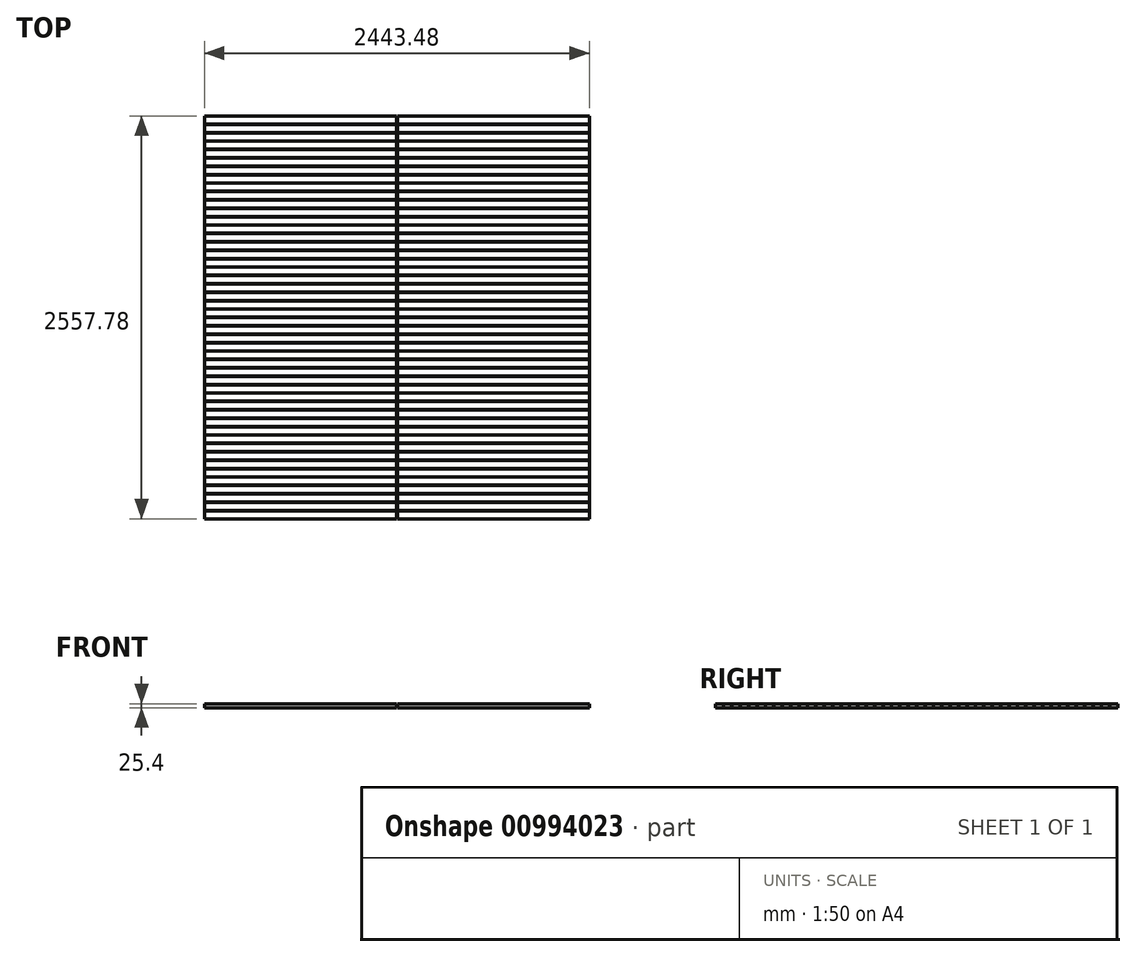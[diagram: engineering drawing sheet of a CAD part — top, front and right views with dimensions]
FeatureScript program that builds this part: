
annotation { "Feature Type Name" : "Feature", "Feature Type Description" : "" }
export const myFeature = defineFeature(function(context is Context, id is Id, definition is map)
    precondition{}
    {
        {
            var Q0;
            Q0=qCreatedBy(makeId("Top.planeOp"),FACE);
            var sketch = newSketch(context, id + "F0", { "sketchPlane" : qUnion([Q0])});
            skLineSegment(sketch, "E0", {"start": v(0, 0) * mm, "end": v(0, 2540) * mm});
            skLineSegment(sketch, "E1.bottom", {"start": v(-1221.74, 2548.89) * mm, "end": v(-2.54, 2548.89) * mm});
            skLineSegment(sketch, "E1.top", {"start": v(-1221.74, 2498.09) * mm, "end": v(-2.54, 2498.09) * mm});
            skLineSegment(sketch, "E1.left", {"start": v(-1221.74, 2548.89) * mm, "end": v(-1221.74, 2498.09) * mm});
            skLineSegment(sketch, "E1.right", {"start": v(-2.54, 2548.89) * mm, "end": v(-2.54, 2498.09) * mm});
            skLineSegment(sketch, "E2.0.1.0", {"start": v(-1221.74, 2495.55) * mm, "end": v(-1221.74, 2444.75) * mm});
            skLineSegment(sketch, "E2.0.1.1", {"start": v(-2.54, 2495.55) * mm, "end": v(-2.54, 2444.75) * mm});
            skLineSegment(sketch, "E2.0.1.2", {"start": v(-1221.74, 2495.55) * mm, "end": v(-2.54, 2495.55) * mm});
            skLineSegment(sketch, "E2.0.1.3", {"start": v(-1221.74, 2444.75) * mm, "end": v(-2.54, 2444.75) * mm});
            skLineSegment(sketch, "E2.0.2.0", {"start": v(-1221.74, 2442.2) * mm, "end": v(-1221.74, 2391.4) * mm});
            skLineSegment(sketch, "E2.0.2.1", {"start": v(-2.54, 2442.2) * mm, "end": v(-2.54, 2391.4) * mm});
            skLineSegment(sketch, "E2.0.2.2", {"start": v(-1221.74, 2442.2) * mm, "end": v(-2.54, 2442.2) * mm});
            skLineSegment(sketch, "E2.0.2.3", {"start": v(-1221.74, 2391.4) * mm, "end": v(-2.54, 2391.4) * mm});
            skLineSegment(sketch, "E2.0.3.0", {"start": v(-1221.74, 2388.87) * mm, "end": v(-1221.74, 2338.07) * mm});
            skLineSegment(sketch, "E2.0.3.1", {"start": v(-2.54, 2388.87) * mm, "end": v(-2.54, 2338.07) * mm});
            skLineSegment(sketch, "E2.0.3.2", {"start": v(-1221.74, 2388.87) * mm, "end": v(-2.54, 2388.87) * mm});
            skLineSegment(sketch, "E2.0.3.3", {"start": v(-1221.74, 2338.07) * mm, "end": v(-2.54, 2338.07) * mm});
            skLineSegment(sketch, "E2.0.4.0", {"start": v(-1221.74, 2335.53) * mm, "end": v(-1221.74, 2284.73) * mm});
            skLineSegment(sketch, "E2.0.4.1", {"start": v(-2.54, 2335.53) * mm, "end": v(-2.54, 2284.73) * mm});
            skLineSegment(sketch, "E2.0.4.2", {"start": v(-1221.74, 2335.53) * mm, "end": v(-2.54, 2335.53) * mm});
            skLineSegment(sketch, "E2.0.4.3", {"start": v(-1221.74, 2284.73) * mm, "end": v(-2.54, 2284.73) * mm});
            skLineSegment(sketch, "E2.0.5.0", {"start": v(-1221.74, 2282.2) * mm, "end": v(-1221.74, 2231.39) * mm});
            skLineSegment(sketch, "E2.0.5.1", {"start": v(-2.54, 2282.2) * mm, "end": v(-2.54, 2231.39) * mm});
            skLineSegment(sketch, "E2.0.5.2", {"start": v(-1221.74, 2282.2) * mm, "end": v(-2.54, 2282.2) * mm});
            skLineSegment(sketch, "E2.0.5.3", {"start": v(-1221.74, 2231.39) * mm, "end": v(-2.54, 2231.39) * mm});
            skLineSegment(sketch, "E2.0.6.0", {"start": v(-1221.74, 2228.85) * mm, "end": v(-1221.74, 2178.05) * mm});
            skLineSegment(sketch, "E2.0.6.1", {"start": v(-2.54, 2228.85) * mm, "end": v(-2.54, 2178.05) * mm});
            skLineSegment(sketch, "E2.0.6.2", {"start": v(-1221.74, 2228.85) * mm, "end": v(-2.54, 2228.85) * mm});
            skLineSegment(sketch, "E2.0.6.3", {"start": v(-1221.74, 2178.05) * mm, "end": v(-2.54, 2178.05) * mm});
            skLineSegment(sketch, "E2.0.7.0", {"start": v(-1221.74, 2175.51) * mm, "end": v(-1221.74, 2124.7) * mm});
            skLineSegment(sketch, "E2.0.7.1", {"start": v(-2.54, 2175.51) * mm, "end": v(-2.54, 2124.7) * mm});
            skLineSegment(sketch, "E2.0.7.2", {"start": v(-1221.74, 2175.51) * mm, "end": v(-2.54, 2175.51) * mm});
            skLineSegment(sketch, "E2.0.7.3", {"start": v(-1221.74, 2124.7) * mm, "end": v(-2.54, 2124.7) * mm});
            skLineSegment(sketch, "E2.0.8.0", {"start": v(-1221.74, 2122.17) * mm, "end": v(-1221.74, 2071.37) * mm});
            skLineSegment(sketch, "E2.0.8.1", {"start": v(-2.54, 2122.17) * mm, "end": v(-2.54, 2071.37) * mm});
            skLineSegment(sketch, "E2.0.8.2", {"start": v(-1221.74, 2122.17) * mm, "end": v(-2.54, 2122.17) * mm});
            skLineSegment(sketch, "E2.0.8.3", {"start": v(-1221.74, 2071.37) * mm, "end": v(-2.54, 2071.37) * mm});
            skLineSegment(sketch, "E2.0.9.0", {"start": v(-1221.74, 2068.83) * mm, "end": v(-1221.74, 2018.03) * mm});
            skLineSegment(sketch, "E2.0.9.1", {"start": v(-2.54, 2068.83) * mm, "end": v(-2.54, 2018.03) * mm});
            skLineSegment(sketch, "E2.0.9.2", {"start": v(-1221.74, 2068.83) * mm, "end": v(-2.54, 2068.83) * mm});
            skLineSegment(sketch, "E2.0.9.3", {"start": v(-1221.74, 2018.03) * mm, "end": v(-2.54, 2018.03) * mm});
            skLineSegment(sketch, "E2.0.10.0", {"start": v(-1221.74, 2015.5) * mm, "end": v(-1221.74, 1964.69) * mm});
            skLineSegment(sketch, "E2.0.10.1", {"start": v(-2.54, 2015.5) * mm, "end": v(-2.54, 1964.69) * mm});
            skLineSegment(sketch, "E2.0.10.2", {"start": v(-1221.74, 2015.5) * mm, "end": v(-2.54, 2015.5) * mm});
            skLineSegment(sketch, "E2.0.10.3", {"start": v(-1221.74, 1964.69) * mm, "end": v(-2.54, 1964.7) * mm});
            skLineSegment(sketch, "E2.0.11.0", {"start": v(-1221.74, 1962.15) * mm, "end": v(-1221.74, 1911.35) * mm});
            skLineSegment(sketch, "E2.0.11.1", {"start": v(-2.54, 1962.15) * mm, "end": v(-2.54, 1911.35) * mm});
            skLineSegment(sketch, "E2.0.11.2", {"start": v(-1221.74, 1962.15) * mm, "end": v(-2.54, 1962.15) * mm});
            skLineSegment(sketch, "E2.0.11.3", {"start": v(-1221.74, 1911.35) * mm, "end": v(-2.54, 1911.35) * mm});
            skLineSegment(sketch, "E2.0.12.0", {"start": v(-1221.74, 1908.81) * mm, "end": v(-1221.74, 1858) * mm});
            skLineSegment(sketch, "E2.0.12.1", {"start": v(-2.54, 1908.81) * mm, "end": v(-2.54, 1858) * mm});
            skLineSegment(sketch, "E2.0.12.2", {"start": v(-1221.74, 1908.81) * mm, "end": v(-2.54, 1908.81) * mm});
            skLineSegment(sketch, "E2.0.12.3", {"start": v(-1221.74, 1858) * mm, "end": v(-2.54, 1858.01) * mm});
            skLineSegment(sketch, "E2.0.13.0", {"start": v(-1221.74, 1855.47) * mm, "end": v(-1221.74, 1804.67) * mm});
            skLineSegment(sketch, "E2.0.13.1", {"start": v(-2.54, 1855.47) * mm, "end": v(-2.54, 1804.67) * mm});
            skLineSegment(sketch, "E2.0.13.2", {"start": v(-1221.74, 1855.47) * mm, "end": v(-2.54, 1855.47) * mm});
            skLineSegment(sketch, "E2.0.13.3", {"start": v(-1221.74, 1804.67) * mm, "end": v(-2.54, 1804.67) * mm});
            skLineSegment(sketch, "E2.0.14.0", {"start": v(-1221.74, 1802.13) * mm, "end": v(-1221.74, 1751.33) * mm});
            skLineSegment(sketch, "E2.0.14.1", {"start": v(-2.54, 1802.13) * mm, "end": v(-2.54, 1751.33) * mm});
            skLineSegment(sketch, "E2.0.14.2", {"start": v(-1221.74, 1802.13) * mm, "end": v(-2.54, 1802.13) * mm});
            skLineSegment(sketch, "E2.0.14.3", {"start": v(-1221.74, 1751.33) * mm, "end": v(-2.54, 1751.33) * mm});
            skLineSegment(sketch, "E2.0.15.0", {"start": v(-1221.74, 1748.8) * mm, "end": v(-1221.74, 1698) * mm});
            skLineSegment(sketch, "E2.0.15.1", {"start": v(-2.54, 1748.8) * mm, "end": v(-2.54, 1698) * mm});
            skLineSegment(sketch, "E2.0.15.2", {"start": v(-1221.74, 1748.8) * mm, "end": v(-2.54, 1748.8) * mm});
            skLineSegment(sketch, "E2.0.15.3", {"start": v(-1221.74, 1698) * mm, "end": v(-2.54, 1698) * mm});
            skLineSegment(sketch, "E2.0.16.0", {"start": v(-1221.74, 1695.45) * mm, "end": v(-1221.74, 1644.65) * mm});
            skLineSegment(sketch, "E2.0.16.1", {"start": v(-2.54, 1695.45) * mm, "end": v(-2.54, 1644.65) * mm});
            skLineSegment(sketch, "E2.0.16.2", {"start": v(-1221.74, 1695.45) * mm, "end": v(-2.54, 1695.45) * mm});
            skLineSegment(sketch, "E2.0.16.3", {"start": v(-1221.74, 1644.65) * mm, "end": v(-2.54, 1644.65) * mm});
            skLineSegment(sketch, "E2.0.17.0", {"start": v(-1221.74, 1642.11) * mm, "end": v(-1221.74, 1591.31) * mm});
            skLineSegment(sketch, "E2.0.17.1", {"start": v(-2.54, 1642.11) * mm, "end": v(-2.54, 1591.31) * mm});
            skLineSegment(sketch, "E2.0.17.2", {"start": v(-1221.74, 1642.11) * mm, "end": v(-2.54, 1642.11) * mm});
            skLineSegment(sketch, "E2.0.17.3", {"start": v(-1221.74, 1591.31) * mm, "end": v(-2.54, 1591.31) * mm});
            skLineSegment(sketch, "E2.0.18.0", {"start": v(-1221.74, 1588.77) * mm, "end": v(-1221.74, 1537.97) * mm});
            skLineSegment(sketch, "E2.0.18.1", {"start": v(-2.54, 1588.77) * mm, "end": v(-2.54, 1537.97) * mm});
            skLineSegment(sketch, "E2.0.18.2", {"start": v(-1221.74, 1588.77) * mm, "end": v(-2.54, 1588.77) * mm});
            skLineSegment(sketch, "E2.0.18.3", {"start": v(-1221.74, 1537.97) * mm, "end": v(-2.54, 1537.97) * mm});
            skLineSegment(sketch, "E2.0.19.0", {"start": v(-1221.74, 1535.43) * mm, "end": v(-1221.74, 1484.63) * mm});
            skLineSegment(sketch, "E2.0.19.1", {"start": v(-2.54, 1535.43) * mm, "end": v(-2.54, 1484.63) * mm});
            skLineSegment(sketch, "E2.0.19.2", {"start": v(-1221.74, 1535.43) * mm, "end": v(-2.54, 1535.43) * mm});
            skLineSegment(sketch, "E2.0.19.3", {"start": v(-1221.74, 1484.63) * mm, "end": v(-2.54, 1484.63) * mm});
            skLineSegment(sketch, "E2.0.20.0", {"start": v(-1221.74, 1482.1) * mm, "end": v(-1221.74, 1431.3) * mm});
            skLineSegment(sketch, "E2.0.20.1", {"start": v(-2.54, 1482.1) * mm, "end": v(-2.54, 1431.3) * mm});
            skLineSegment(sketch, "E2.0.20.2", {"start": v(-1221.74, 1482.1) * mm, "end": v(-2.54, 1482.1) * mm});
            skLineSegment(sketch, "E2.0.20.3", {"start": v(-1221.74, 1431.3) * mm, "end": v(-2.54, 1431.3) * mm});
            skLineSegment(sketch, "E2.0.21.0", {"start": v(-1221.74, 1428.75) * mm, "end": v(-1221.74, 1377.95) * mm});
            skLineSegment(sketch, "E2.0.21.1", {"start": v(-2.54, 1428.75) * mm, "end": v(-2.54, 1377.95) * mm});
            skLineSegment(sketch, "E2.0.21.2", {"start": v(-1221.74, 1428.75) * mm, "end": v(-2.54, 1428.75) * mm});
            skLineSegment(sketch, "E2.0.21.3", {"start": v(-1221.74, 1377.95) * mm, "end": v(-2.54, 1377.95) * mm});
            skLineSegment(sketch, "E2.0.22.0", {"start": v(-1221.74, 1375.41) * mm, "end": v(-1221.74, 1324.61) * mm});
            skLineSegment(sketch, "E2.0.22.1", {"start": v(-2.54, 1375.41) * mm, "end": v(-2.54, 1324.61) * mm});
            skLineSegment(sketch, "E2.0.22.2", {"start": v(-1221.74, 1375.41) * mm, "end": v(-2.54, 1375.41) * mm});
            skLineSegment(sketch, "E2.0.22.3", {"start": v(-1221.74, 1324.61) * mm, "end": v(-2.54, 1324.61) * mm});
            skLineSegment(sketch, "E2.0.23.0", {"start": v(-1221.74, 1322.07) * mm, "end": v(-1221.74, 1271.27) * mm});
            skLineSegment(sketch, "E2.0.23.1", {"start": v(-2.54, 1322.07) * mm, "end": v(-2.54, 1271.27) * mm});
            skLineSegment(sketch, "E2.0.23.2", {"start": v(-1221.74, 1322.07) * mm, "end": v(-2.54, 1322.07) * mm});
            skLineSegment(sketch, "E2.0.23.3", {"start": v(-1221.74, 1271.27) * mm, "end": v(-2.54, 1271.27) * mm});
            skLineSegment(sketch, "E2.0.24.0", {"start": v(-1221.74, 1268.73) * mm, "end": v(-1221.74, 1217.93) * mm});
            skLineSegment(sketch, "E2.0.24.1", {"start": v(-2.54, 1268.73) * mm, "end": v(-2.54, 1217.93) * mm});
            skLineSegment(sketch, "E2.0.24.2", {"start": v(-1221.74, 1268.73) * mm, "end": v(-2.54, 1268.73) * mm});
            skLineSegment(sketch, "E2.0.24.3", {"start": v(-1221.74, 1217.93) * mm, "end": v(-2.54, 1217.93) * mm});
            skLineSegment(sketch, "E2.0.25.0", {"start": v(-1221.74, 1215.4) * mm, "end": v(-1221.74, 1164.6) * mm});
            skLineSegment(sketch, "E2.0.25.1", {"start": v(-2.54, 1215.4) * mm, "end": v(-2.54, 1164.6) * mm});
            skLineSegment(sketch, "E2.0.25.2", {"start": v(-1221.74, 1215.4) * mm, "end": v(-2.54, 1215.4) * mm});
            skLineSegment(sketch, "E2.0.25.3", {"start": v(-1221.74, 1164.6) * mm, "end": v(-2.54, 1164.6) * mm});
            skLineSegment(sketch, "E2.0.26.0", {"start": v(-1221.74, 1162.05) * mm, "end": v(-1221.74, 1111.25) * mm});
            skLineSegment(sketch, "E2.0.26.1", {"start": v(-2.54, 1162.05) * mm, "end": v(-2.54, 1111.25) * mm});
            skLineSegment(sketch, "E2.0.26.2", {"start": v(-1221.74, 1162.05) * mm, "end": v(-2.54, 1162.05) * mm});
            skLineSegment(sketch, "E2.0.26.3", {"start": v(-1221.74, 1111.25) * mm, "end": v(-2.54, 1111.25) * mm});
            skLineSegment(sketch, "E2.0.27.0", {"start": v(-1221.74, 1108.71) * mm, "end": v(-1221.74, 1057.91) * mm});
            skLineSegment(sketch, "E2.0.27.1", {"start": v(-2.54, 1108.71) * mm, "end": v(-2.54, 1057.91) * mm});
            skLineSegment(sketch, "E2.0.27.2", {"start": v(-1221.74, 1108.71) * mm, "end": v(-2.54, 1108.71) * mm});
            skLineSegment(sketch, "E2.0.27.3", {"start": v(-1221.74, 1057.91) * mm, "end": v(-2.54, 1057.91) * mm});
            skLineSegment(sketch, "E2.0.28.0", {"start": v(-1221.74, 1055.37) * mm, "end": v(-1221.74, 1004.57) * mm});
            skLineSegment(sketch, "E2.0.28.1", {"start": v(-2.54, 1055.37) * mm, "end": v(-2.54, 1004.57) * mm});
            skLineSegment(sketch, "E2.0.28.2", {"start": v(-1221.74, 1055.37) * mm, "end": v(-2.54, 1055.37) * mm});
            skLineSegment(sketch, "E2.0.28.3", {"start": v(-1221.74, 1004.57) * mm, "end": v(-2.54, 1004.57) * mm});
            skLineSegment(sketch, "E2.0.29.0", {"start": v(-1221.74, 1002.03) * mm, "end": v(-1221.74, 951.23) * mm});
            skLineSegment(sketch, "E2.0.29.1", {"start": v(-2.54, 1002.03) * mm, "end": v(-2.54, 951.23) * mm});
            skLineSegment(sketch, "E2.0.29.2", {"start": v(-1221.74, 1002.03) * mm, "end": v(-2.54, 1002.03) * mm});
            skLineSegment(sketch, "E2.0.29.3", {"start": v(-1221.74, 951.23) * mm, "end": v(-2.54, 951.23) * mm});
            skLineSegment(sketch, "E2.0.30.0", {"start": v(-1221.74, 948.7) * mm, "end": v(-1221.74, 897.9) * mm});
            skLineSegment(sketch, "E2.0.30.1", {"start": v(-2.54, 948.7) * mm, "end": v(-2.54, 897.9) * mm});
            skLineSegment(sketch, "E2.0.30.2", {"start": v(-1221.74, 948.7) * mm, "end": v(-2.54, 948.7) * mm});
            skLineSegment(sketch, "E2.0.30.3", {"start": v(-1221.74, 897.9) * mm, "end": v(-2.54, 897.9) * mm});
            skLineSegment(sketch, "E2.0.31.0", {"start": v(-1221.74, 895.35) * mm, "end": v(-1221.74, 844.55) * mm});
            skLineSegment(sketch, "E2.0.31.1", {"start": v(-2.54, 895.35) * mm, "end": v(-2.54, 844.55) * mm});
            skLineSegment(sketch, "E2.0.31.2", {"start": v(-1221.74, 895.35) * mm, "end": v(-2.54, 895.35) * mm});
            skLineSegment(sketch, "E2.0.31.3", {"start": v(-1221.74, 844.55) * mm, "end": v(-2.54, 844.55) * mm});
            skLineSegment(sketch, "E2.0.32.0", {"start": v(-1221.74, 842.01) * mm, "end": v(-1221.74, 791.21) * mm});
            skLineSegment(sketch, "E2.0.32.1", {"start": v(-2.54, 842.01) * mm, "end": v(-2.54, 791.21) * mm});
            skLineSegment(sketch, "E2.0.32.2", {"start": v(-1221.74, 842.01) * mm, "end": v(-2.54, 842.01) * mm});
            skLineSegment(sketch, "E2.0.32.3", {"start": v(-1221.74, 791.21) * mm, "end": v(-2.54, 791.21) * mm});
            skLineSegment(sketch, "E2.0.33.0", {"start": v(-1221.74, 788.67) * mm, "end": v(-1221.74, 737.87) * mm});
            skLineSegment(sketch, "E2.0.33.1", {"start": v(-2.54, 788.67) * mm, "end": v(-2.54, 737.87) * mm});
            skLineSegment(sketch, "E2.0.33.2", {"start": v(-1221.74, 788.67) * mm, "end": v(-2.54, 788.67) * mm});
            skLineSegment(sketch, "E2.0.33.3", {"start": v(-1221.74, 737.87) * mm, "end": v(-2.54, 737.87) * mm});
            skLineSegment(sketch, "E2.0.34.0", {"start": v(-1221.74, 735.33) * mm, "end": v(-1221.74, 684.53) * mm});
            skLineSegment(sketch, "E2.0.34.1", {"start": v(-2.54, 735.33) * mm, "end": v(-2.54, 684.53) * mm});
            skLineSegment(sketch, "E2.0.34.2", {"start": v(-1221.74, 735.33) * mm, "end": v(-2.54, 735.33) * mm});
            skLineSegment(sketch, "E2.0.34.3", {"start": v(-1221.74, 684.53) * mm, "end": v(-2.54, 684.53) * mm});
            skLineSegment(sketch, "E2.0.35.0", {"start": v(-1221.74, 682) * mm, "end": v(-1221.74, 631.2) * mm});
            skLineSegment(sketch, "E2.0.35.1", {"start": v(-2.54, 682) * mm, "end": v(-2.54, 631.2) * mm});
            skLineSegment(sketch, "E2.0.35.2", {"start": v(-1221.74, 682) * mm, "end": v(-2.54, 682) * mm});
            skLineSegment(sketch, "E2.0.35.3", {"start": v(-1221.74, 631.2) * mm, "end": v(-2.54, 631.2) * mm});
            skLineSegment(sketch, "E2.0.36.0", {"start": v(-1221.74, 628.65) * mm, "end": v(-1221.74, 577.85) * mm});
            skLineSegment(sketch, "E2.0.36.1", {"start": v(-2.54, 628.65) * mm, "end": v(-2.54, 577.85) * mm});
            skLineSegment(sketch, "E2.0.36.2", {"start": v(-1221.74, 628.65) * mm, "end": v(-2.54, 628.65) * mm});
            skLineSegment(sketch, "E2.0.36.3", {"start": v(-1221.74, 577.85) * mm, "end": v(-2.54, 577.85) * mm});
            skLineSegment(sketch, "E2.0.37.0", {"start": v(-1221.74, 575.31) * mm, "end": v(-1221.74, 524.51) * mm});
            skLineSegment(sketch, "E2.0.37.1", {"start": v(-2.54, 575.31) * mm, "end": v(-2.54, 524.51) * mm});
            skLineSegment(sketch, "E2.0.37.2", {"start": v(-1221.74, 575.31) * mm, "end": v(-2.54, 575.31) * mm});
            skLineSegment(sketch, "E2.0.37.3", {"start": v(-1221.74, 524.51) * mm, "end": v(-2.54, 524.51) * mm});
            skLineSegment(sketch, "E2.0.38.0", {"start": v(-1221.74, 521.97) * mm, "end": v(-1221.74, 471.17) * mm});
            skLineSegment(sketch, "E2.0.38.1", {"start": v(-2.54, 521.97) * mm, "end": v(-2.54, 471.17) * mm});
            skLineSegment(sketch, "E2.0.38.2", {"start": v(-1221.74, 521.97) * mm, "end": v(-2.54, 521.97) * mm});
            skLineSegment(sketch, "E2.0.38.3", {"start": v(-1221.74, 471.17) * mm, "end": v(-2.54, 471.17) * mm});
            skLineSegment(sketch, "E2.0.39.0", {"start": v(-1221.74, 468.63) * mm, "end": v(-1221.74, 417.83) * mm});
            skLineSegment(sketch, "E2.0.39.1", {"start": v(-2.54, 468.63) * mm, "end": v(-2.54, 417.83) * mm});
            skLineSegment(sketch, "E2.0.39.2", {"start": v(-1221.74, 468.63) * mm, "end": v(-2.54, 468.63) * mm});
            skLineSegment(sketch, "E2.0.39.3", {"start": v(-1221.74, 417.83) * mm, "end": v(-2.54, 417.83) * mm});
            skLineSegment(sketch, "E2.0.40.0", {"start": v(-1221.74, 415.3) * mm, "end": v(-1221.74, 364.5) * mm});
            skLineSegment(sketch, "E2.0.40.1", {"start": v(-2.54, 415.3) * mm, "end": v(-2.54, 364.5) * mm});
            skLineSegment(sketch, "E2.0.40.2", {"start": v(-1221.74, 415.3) * mm, "end": v(-2.54, 415.3) * mm});
            skLineSegment(sketch, "E2.0.40.3", {"start": v(-1221.74, 364.5) * mm, "end": v(-2.54, 364.5) * mm});
            skLineSegment(sketch, "E2.0.41.0", {"start": v(-1221.74, 361.95) * mm, "end": v(-1221.74, 311.15) * mm});
            skLineSegment(sketch, "E2.0.41.1", {"start": v(-2.54, 361.95) * mm, "end": v(-2.54, 311.15) * mm});
            skLineSegment(sketch, "E2.0.41.2", {"start": v(-1221.74, 361.95) * mm, "end": v(-2.54, 361.95) * mm});
            skLineSegment(sketch, "E2.0.41.3", {"start": v(-1221.74, 311.15) * mm, "end": v(-2.54, 311.15) * mm});
            skLineSegment(sketch, "E2.0.42.0", {"start": v(-1221.74, 308.61) * mm, "end": v(-1221.74, 257.81) * mm});
            skLineSegment(sketch, "E2.0.42.1", {"start": v(-2.54, 308.61) * mm, "end": v(-2.54, 257.81) * mm});
            skLineSegment(sketch, "E2.0.42.2", {"start": v(-1221.74, 308.61) * mm, "end": v(-2.54, 308.61) * mm});
            skLineSegment(sketch, "E2.0.42.3", {"start": v(-1221.74, 257.81) * mm, "end": v(-2.54, 257.81) * mm});
            skLineSegment(sketch, "E2.0.43.0", {"start": v(-1221.74, 255.27) * mm, "end": v(-1221.74, 204.47) * mm});
            skLineSegment(sketch, "E2.0.43.1", {"start": v(-2.54, 255.27) * mm, "end": v(-2.54, 204.47) * mm});
            skLineSegment(sketch, "E2.0.43.2", {"start": v(-1221.74, 255.27) * mm, "end": v(-2.54, 255.27) * mm});
            skLineSegment(sketch, "E2.0.43.3", {"start": v(-1221.74, 204.47) * mm, "end": v(-2.54, 204.47) * mm});
            skLineSegment(sketch, "E2.0.44.0", {"start": v(-1221.74, 201.93) * mm, "end": v(-1221.74, 151.13) * mm});
            skLineSegment(sketch, "E2.0.44.1", {"start": v(-2.54, 201.93) * mm, "end": v(-2.54, 151.13) * mm});
            skLineSegment(sketch, "E2.0.44.2", {"start": v(-1221.74, 201.93) * mm, "end": v(-2.54, 201.93) * mm});
            skLineSegment(sketch, "E2.0.44.3", {"start": v(-1221.74, 151.13) * mm, "end": v(-2.54, 151.13) * mm});
            skLineSegment(sketch, "E2.0.45.0", {"start": v(-1221.74, 148.6) * mm, "end": v(-1221.74, 97.8) * mm});
            skLineSegment(sketch, "E2.0.45.1", {"start": v(-2.54, 148.6) * mm, "end": v(-2.54, 97.8) * mm});
            skLineSegment(sketch, "E2.0.45.2", {"start": v(-1221.74, 148.6) * mm, "end": v(-2.54, 148.6) * mm});
            skLineSegment(sketch, "E2.0.45.3", {"start": v(-1221.74, 97.8) * mm, "end": v(-2.54, 97.8) * mm});
            skLineSegment(sketch, "E2.0.46.0", {"start": v(-1221.74, 95.25) * mm, "end": v(-1221.74, 44.45) * mm});
            skLineSegment(sketch, "E2.0.46.1", {"start": v(-2.54, 95.25) * mm, "end": v(-2.54, 44.45) * mm});
            skLineSegment(sketch, "E2.0.46.2", {"start": v(-1221.74, 95.25) * mm, "end": v(-2.54, 95.25) * mm});
            skLineSegment(sketch, "E2.0.46.3", {"start": v(-1221.74, 44.45) * mm, "end": v(-2.54, 44.45) * mm});
            skLineSegment(sketch, "E2.0.47.0", {"start": v(-1221.74, 41.91) * mm, "end": v(-1221.74, -8.89) * mm});
            skLineSegment(sketch, "E2.0.47.1", {"start": v(-2.54, 41.91) * mm, "end": v(-2.54, -8.89) * mm});
            skLineSegment(sketch, "E2.0.47.2", {"start": v(-1221.74, 41.91) * mm, "end": v(-2.54, 41.91) * mm});
            skLineSegment(sketch, "E2.0.47.3", {"start": v(-1221.74, -8.89) * mm, "end": v(-2.54, -8.89) * mm});
            skLineSegment(sketch, "E2.direction1", {"start": v(-1221.74, 2498.09) * mm, "end": v(-1221.74, 2498.09) * mm});
            skLineSegment(sketch, "E2.direction2", {"start": v(-1221.74, 2498.09) * mm, "end": v(-1221.74, 2444.75) * mm, "construction": true});
            skLineSegment(sketch, "E3.MirrorCS", {"start": v(1221.74, 2388.87) * mm, "end": v(1221.74, 2338.07) * mm});
            skLineSegment(sketch, "E4.MirrorCS", {"start": v(1221.74, 2442.2) * mm, "end": v(1221.74, 2391.4) * mm});
            skLineSegment(sketch, "E5.MirrorCS", {"start": v(1221.74, 2495.55) * mm, "end": v(1221.74, 2444.75) * mm});
            skLineSegment(sketch, "E6.MirrorCS", {"start": v(2.54, 255.27) * mm, "end": v(2.54, 204.47) * mm});
            skLineSegment(sketch, "E7.MirrorCS", {"start": v(1221.74, 1535.43) * mm, "end": v(1221.74, 1484.63) * mm});
            skLineSegment(sketch, "E8.MirrorCS", {"start": v(2.54, 2175.51) * mm, "end": v(2.54, 2124.7) * mm});
            skLineSegment(sketch, "E9.MirrorCS", {"start": v(1221.74, 2228.85) * mm, "end": v(1221.74, 2178.05) * mm});
            skLineSegment(sketch, "E10.MirrorCS", {"start": v(2.54, 468.63) * mm, "end": v(2.54, 417.83) * mm});
            skLineSegment(sketch, "E11.MirrorCS", {"start": v(2.54, 1055.37) * mm, "end": v(2.54, 1004.57) * mm});
            skLineSegment(sketch, "E12.MirrorCS", {"start": v(1221.74, 948.7) * mm, "end": v(1221.74, 897.9) * mm});
            skLineSegment(sketch, "E13.MirrorCS", {"start": v(1221.74, 735.33) * mm, "end": v(1221.74, 684.53) * mm});
            skLineSegment(sketch, "E14.MirrorCS", {"start": v(1221.74, 2175.51) * mm, "end": v(1221.74, 2124.7) * mm});
            skLineSegment(sketch, "E15.MirrorCS", {"start": v(2.54, 1642.11) * mm, "end": v(2.54, 1591.31) * mm});
            skLineSegment(sketch, "E16.MirrorCS", {"start": v(2.54, 1108.71) * mm, "end": v(2.54, 1057.91) * mm});
            skLineSegment(sketch, "E17.MirrorCS", {"start": v(1221.74, 682) * mm, "end": v(1221.74, 631.2) * mm});
            skLineSegment(sketch, "E18.MirrorCS", {"start": v(1221.74, 2498.09) * mm, "end": v(1221.74, 2444.75) * mm, "construction": true});
            skLineSegment(sketch, "E19.MirrorCS", {"start": v(1221.74, 2335.53) * mm, "end": v(1221.74, 2284.73) * mm});
            skLineSegment(sketch, "E20.MirrorCS", {"start": v(2.54, 1908.81) * mm, "end": v(2.54, 1858) * mm});
            skLineSegment(sketch, "E21.MirrorCS", {"start": v(2.54, 415.3) * mm, "end": v(2.54, 364.5) * mm});
            skLineSegment(sketch, "E22.MirrorCS", {"start": v(1221.74, 255.27) * mm, "end": v(1221.74, 204.47) * mm});
            skLineSegment(sketch, "E23.MirrorCS", {"start": v(2.54, 1482.1) * mm, "end": v(2.54, 1431.3) * mm});
            skLineSegment(sketch, "E24.MirrorCS", {"start": v(2.54, 2388.87) * mm, "end": v(2.54, 2338.07) * mm});
            skLineSegment(sketch, "E25.MirrorCS", {"start": v(2.54, 2335.53) * mm, "end": v(2.54, 2284.73) * mm});
            skLineSegment(sketch, "E26.MirrorCS", {"start": v(1221.74, 521.97) * mm, "end": v(1221.74, 471.17) * mm});
            skLineSegment(sketch, "E27.MirrorCS", {"start": v(1221.74, 1108.71) * mm, "end": v(1221.74, 1057.91) * mm});
            skLineSegment(sketch, "E28.MirrorCS", {"start": v(2.54, 361.95) * mm, "end": v(2.54, 311.15) * mm});
            skLineSegment(sketch, "E29.MirrorCS", {"start": v(1221.74, 1322.07) * mm, "end": v(1221.74, 1271.27) * mm});
            skLineSegment(sketch, "E30.MirrorCS", {"start": v(2.54, 2122.17) * mm, "end": v(2.54, 2071.37) * mm});
            skLineSegment(sketch, "E31.MirrorCS", {"start": v(1221.74, 1375.41) * mm, "end": v(1221.74, 1324.61) * mm});
            skLineSegment(sketch, "E32.MirrorCS", {"start": v(1221.74, 2015.5) * mm, "end": v(1221.74, 1964.69) * mm});
            skLineSegment(sketch, "E33.MirrorCS", {"start": v(2.54, 842.01) * mm, "end": v(2.54, 791.21) * mm});
            skLineSegment(sketch, "E34.MirrorCS", {"start": v(2.54, 788.67) * mm, "end": v(2.54, 737.87) * mm});
            skLineSegment(sketch, "E35.MirrorCS", {"start": v(2.54, 895.35) * mm, "end": v(2.54, 844.55) * mm});
            skLineSegment(sketch, "E36.MirrorCS", {"start": v(2.54, 1588.77) * mm, "end": v(2.54, 1537.97) * mm});
            skLineSegment(sketch, "E37.MirrorCS", {"start": v(2.54, 201.93) * mm, "end": v(2.54, 151.13) * mm});
            skLineSegment(sketch, "E38.MirrorCS", {"start": v(2.54, 1535.43) * mm, "end": v(2.54, 1484.63) * mm});
            skLineSegment(sketch, "E39.MirrorCS", {"start": v(1221.74, 1162.05) * mm, "end": v(1221.74, 1111.25) * mm});
            skLineSegment(sketch, "E40.MirrorCS", {"start": v(1221.74, 468.63) * mm, "end": v(1221.74, 417.83) * mm});
            skLineSegment(sketch, "E41.MirrorCS", {"start": v(2.54, 1748.8) * mm, "end": v(2.54, 1698) * mm});
            skLineSegment(sketch, "E42.MirrorCS", {"start": v(2.54, 682) * mm, "end": v(2.54, 631.2) * mm});
            skLineSegment(sketch, "E43.MirrorCS", {"start": v(2.54, 308.61) * mm, "end": v(2.54, 257.81) * mm});
            skLineSegment(sketch, "E44.MirrorCS", {"start": v(1221.74, 1748.8) * mm, "end": v(1221.74, 1698) * mm});
            skLineSegment(sketch, "E45.MirrorCS", {"start": v(1221.74, 1802.13) * mm, "end": v(1221.74, 1751.33) * mm});
            skLineSegment(sketch, "E46.MirrorCS", {"start": v(1221.74, 1962.15) * mm, "end": v(1221.74, 1911.35) * mm});
            skLineSegment(sketch, "E47.MirrorCS", {"start": v(2.54, 1322.07) * mm, "end": v(2.54, 1271.27) * mm});
            skLineSegment(sketch, "E48.MirrorCS", {"start": v(1221.74, 895.35) * mm, "end": v(1221.74, 844.55) * mm});
            skLineSegment(sketch, "E49.MirrorCS", {"start": v(1221.74, 1588.77) * mm, "end": v(1221.74, 1537.97) * mm});
            skLineSegment(sketch, "E50.MirrorCS", {"start": v(2.54, 628.65) * mm, "end": v(2.54, 577.85) * mm});
            skLineSegment(sketch, "E51.MirrorCS", {"start": v(2.54, 1268.73) * mm, "end": v(2.54, 1217.93) * mm});
            skLineSegment(sketch, "E52.MirrorCS", {"start": v(1221.74, 2548.89) * mm, "end": v(1221.74, 2498.09) * mm});
            skLineSegment(sketch, "E53.MirrorCS", {"start": v(2.54, 2442.2) * mm, "end": v(2.54, 2391.4) * mm});
            skLineSegment(sketch, "E54.MirrorCS", {"start": v(2.54, 575.31) * mm, "end": v(2.54, 524.51) * mm});
            skLineSegment(sketch, "E55.MirrorCS", {"start": v(2.54, 1962.15) * mm, "end": v(2.54, 1911.35) * mm});
            skLineSegment(sketch, "E56.MirrorCS", {"start": v(2.54, 1802.13) * mm, "end": v(2.54, 1751.33) * mm});
            skLineSegment(sketch, "E57.MirrorCS", {"start": v(2.54, 1695.45) * mm, "end": v(2.54, 1644.65) * mm});
            skLineSegment(sketch, "E58.MirrorCS", {"start": v(2.54, 1855.47) * mm, "end": v(2.54, 1804.67) * mm});
            skLineSegment(sketch, "E59.MirrorCS", {"start": v(1221.74, 308.61) * mm, "end": v(1221.74, 257.81) * mm});
            skLineSegment(sketch, "E60.MirrorCS", {"start": v(2.54, 2282.2) * mm, "end": v(2.54, 2231.39) * mm});
            skLineSegment(sketch, "E61.MirrorCS", {"start": v(1221.74, 2282.2) * mm, "end": v(1221.74, 2231.39) * mm});
            skLineSegment(sketch, "E62.MirrorCS", {"start": v(1221.74, 628.65) * mm, "end": v(1221.74, 577.85) * mm});
            skLineSegment(sketch, "E63.MirrorCS", {"start": v(1221.74, 2068.83) * mm, "end": v(1221.74, 2018.03) * mm});
            skLineSegment(sketch, "E64.MirrorCS", {"start": v(2.54, 1428.75) * mm, "end": v(2.54, 1377.95) * mm});
            skLineSegment(sketch, "E65.MirrorCS", {"start": v(1221.74, 95.25) * mm, "end": v(1221.74, 44.45) * mm});
            skLineSegment(sketch, "E66.MirrorCS", {"start": v(1221.74, 1215.4) * mm, "end": v(1221.74, 1164.6) * mm});
            skLineSegment(sketch, "E67.MirrorCS", {"start": v(1221.74, 148.6) * mm, "end": v(1221.74, 97.8) * mm});
            skLineSegment(sketch, "E68.MirrorCS", {"start": v(2.54, 948.7) * mm, "end": v(2.54, 897.9) * mm});
            skLineSegment(sketch, "E69.MirrorCS", {"start": v(2.54, 1162.05) * mm, "end": v(2.54, 1111.25) * mm});
            skLineSegment(sketch, "E70.MirrorCS", {"start": v(2.54, 1375.41) * mm, "end": v(2.54, 1324.61) * mm});
            skLineSegment(sketch, "E71.MirrorCS", {"start": v(1221.74, 2122.17) * mm, "end": v(1221.74, 2071.37) * mm});
            skLineSegment(sketch, "E72.MirrorCS", {"start": v(2.54, 521.97) * mm, "end": v(2.54, 471.17) * mm});
            skLineSegment(sketch, "E73.MirrorCS", {"start": v(1221.74, 361.95) * mm, "end": v(1221.74, 311.15) * mm});
            skLineSegment(sketch, "E74.MirrorCS", {"start": v(2.54, 2068.83) * mm, "end": v(2.54, 2018.03) * mm});
            skLineSegment(sketch, "E75.MirrorCS", {"start": v(1221.74, 1908.81) * mm, "end": v(1221.74, 1858) * mm});
            skLineSegment(sketch, "E76.MirrorCS", {"start": v(1221.74, 842.01) * mm, "end": v(1221.74, 791.21) * mm});
            skLineSegment(sketch, "E77.MirrorCS", {"start": v(1221.74, 1482.1) * mm, "end": v(1221.74, 1431.3) * mm});
            skLineSegment(sketch, "E78.MirrorCS", {"start": v(1221.74, 1002.03) * mm, "end": v(1221.74, 951.23) * mm});
            skLineSegment(sketch, "E79.MirrorCS", {"start": v(2.54, 1002.03) * mm, "end": v(2.54, 951.23) * mm});
            skLineSegment(sketch, "E80.MirrorCS", {"start": v(2.54, 148.6) * mm, "end": v(2.54, 97.8) * mm});
            skLineSegment(sketch, "E81.MirrorCS", {"start": v(1221.74, 1642.11) * mm, "end": v(1221.74, 1591.31) * mm});
            skLineSegment(sketch, "E82.MirrorCS", {"start": v(1221.74, 1268.73) * mm, "end": v(1221.74, 1217.93) * mm});
            skLineSegment(sketch, "E83.MirrorCS", {"start": v(2.54, 2015.5) * mm, "end": v(2.54, 1964.69) * mm});
            skLineSegment(sketch, "E84.MirrorCS", {"start": v(1221.74, 1695.45) * mm, "end": v(1221.74, 1644.65) * mm});
            skLineSegment(sketch, "E85.MirrorCS", {"start": v(1221.74, 1055.37) * mm, "end": v(1221.74, 1004.57) * mm});
            skLineSegment(sketch, "E86.MirrorCS", {"start": v(1221.74, 1428.75) * mm, "end": v(1221.74, 1377.95) * mm});
            skLineSegment(sketch, "E87.MirrorCS", {"start": v(2.54, 2228.85) * mm, "end": v(2.54, 2178.05) * mm});
            skLineSegment(sketch, "E88.MirrorCS", {"start": v(1221.74, 415.3) * mm, "end": v(1221.74, 364.5) * mm});
            skLineSegment(sketch, "E89.MirrorCS", {"start": v(2.54, 735.33) * mm, "end": v(2.54, 684.53) * mm});
            skLineSegment(sketch, "E90.MirrorCS", {"start": v(2.54, 95.25) * mm, "end": v(2.54, 44.45) * mm});
            skLineSegment(sketch, "E91.MirrorCS", {"start": v(1221.74, 201.93) * mm, "end": v(1221.74, 151.13) * mm});
            skLineSegment(sketch, "E92.MirrorCS", {"start": v(1221.74, 788.67) * mm, "end": v(1221.74, 737.87) * mm});
            skLineSegment(sketch, "E93.MirrorCS", {"start": v(1221.74, 575.31) * mm, "end": v(1221.74, 524.51) * mm});
            skLineSegment(sketch, "E94.MirrorCS", {"start": v(1221.74, 1855.47) * mm, "end": v(1221.74, 1804.67) * mm});
            skLineSegment(sketch, "E95.MirrorCS", {"start": v(2.54, 1215.4) * mm, "end": v(2.54, 1164.6) * mm});
            skLineSegment(sketch, "E96.MirrorCS", {"start": v(2.54, 2548.89) * mm, "end": v(2.54, 2498.09) * mm});
            skLineSegment(sketch, "E97.MirrorCS", {"start": v(2.54, 2495.55) * mm, "end": v(2.54, 2444.75) * mm});
            skLineSegment(sketch, "E98.MirrorCS", {"start": v(2.54, 41.91) * mm, "end": v(2.54, -8.89) * mm});
            skLineSegment(sketch, "E99.MirrorCS", {"start": v(1221.74, 41.91) * mm, "end": v(1221.74, -8.89) * mm});
            skLineSegment(sketch, "E100.MirrorCS", {"start": v(1221.74, 2068.83) * mm, "end": v(2.54, 2068.83) * mm});
            skLineSegment(sketch, "E101.MirrorCS", {"start": v(1221.74, 1268.73) * mm, "end": v(2.54, 1268.73) * mm});
            skLineSegment(sketch, "E102.MirrorCS", {"start": v(1221.74, 255.27) * mm, "end": v(2.54, 255.27) * mm});
            skLineSegment(sketch, "E103.MirrorCS", {"start": v(1221.74, 735.33) * mm, "end": v(2.54, 735.33) * mm});
            skLineSegment(sketch, "E104.MirrorCS", {"start": v(1221.74, 788.67) * mm, "end": v(2.54, 788.67) * mm});
            skLineSegment(sketch, "E105.MirrorCS", {"start": v(1221.74, 1428.75) * mm, "end": v(2.54, 1428.75) * mm});
            skLineSegment(sketch, "E106.MirrorCS", {"start": v(1221.74, 151.13) * mm, "end": v(2.54, 151.13) * mm});
            skLineSegment(sketch, "E107.MirrorCS", {"start": v(1221.74, 201.93) * mm, "end": v(2.54, 201.93) * mm});
            skLineSegment(sketch, "E108.MirrorCS", {"start": v(1221.74, 1162.05) * mm, "end": v(2.54, 1162.05) * mm});
            skLineSegment(sketch, "E109.MirrorCS", {"start": v(1221.74, 682) * mm, "end": v(2.54, 682) * mm});
            skLineSegment(sketch, "E110.MirrorCS", {"start": v(1221.74, 1535.43) * mm, "end": v(2.54, 1535.43) * mm});
            skLineSegment(sketch, "E111.MirrorCS", {"start": v(1221.74, 95.25) * mm, "end": v(2.54, 95.25) * mm});
            skLineSegment(sketch, "E112.MirrorCS", {"start": v(1221.74, 468.63) * mm, "end": v(2.54, 468.63) * mm});
            skLineSegment(sketch, "E113.MirrorCS", {"start": v(1221.74, 1002.03) * mm, "end": v(2.54, 1002.03) * mm});
            skLineSegment(sketch, "E114.MirrorCS", {"start": v(1221.74, 1375.41) * mm, "end": v(2.54, 1375.41) * mm});
            skLineSegment(sketch, "E115.MirrorCS", {"start": v(1221.74, 2015.5) * mm, "end": v(2.54, 2015.5) * mm});
            skLineSegment(sketch, "E116.MirrorCS", {"start": v(1221.74, 2444.75) * mm, "end": v(2.54, 2444.75) * mm});
            skLineSegment(sketch, "E117.MirrorCS", {"start": v(1221.74, 2335.53) * mm, "end": v(2.54, 2335.53) * mm});
            skLineSegment(sketch, "E118.MirrorCS", {"start": v(1221.74, 1588.77) * mm, "end": v(2.54, 1588.77) * mm});
            skLineSegment(sketch, "E119.MirrorCS", {"start": v(1221.74, 2175.51) * mm, "end": v(2.54, 2175.51) * mm});
            skLineSegment(sketch, "E120.MirrorCS", {"start": v(1221.74, 2228.85) * mm, "end": v(2.54, 2228.85) * mm});
            skLineSegment(sketch, "E121.MirrorCS", {"start": v(1221.74, 1108.71) * mm, "end": v(2.54, 1108.71) * mm});
            skLineSegment(sketch, "E122.MirrorCS", {"start": v(1221.74, 2282.2) * mm, "end": v(2.54, 2282.2) * mm});
            skLineSegment(sketch, "E123.MirrorCS", {"start": v(1221.74, 1748.8) * mm, "end": v(2.54, 1748.8) * mm});
            skLineSegment(sketch, "E124.MirrorCS", {"start": v(1221.74, 415.3) * mm, "end": v(2.54, 415.3) * mm});
            skLineSegment(sketch, "E125.MirrorCS", {"start": v(1221.74, 1802.13) * mm, "end": v(2.54, 1802.13) * mm});
            skLineSegment(sketch, "E126.MirrorCS", {"start": v(1221.74, 842.01) * mm, "end": v(2.54, 842.01) * mm});
            skLineSegment(sketch, "E127.MirrorCS", {"start": v(1221.74, 1962.15) * mm, "end": v(2.54, 1962.15) * mm});
            skLineSegment(sketch, "E128.MirrorCS", {"start": v(1221.74, 1695.45) * mm, "end": v(2.54, 1695.45) * mm});
            skLineSegment(sketch, "E129.MirrorCS", {"start": v(1221.74, 308.61) * mm, "end": v(2.54, 308.61) * mm});
            skLineSegment(sketch, "E130.MirrorCS", {"start": v(1221.74, 1642.11) * mm, "end": v(2.54, 1642.11) * mm});
            skLineSegment(sketch, "E131.MirrorCS", {"start": v(1221.74, 521.97) * mm, "end": v(2.54, 521.97) * mm});
            skLineSegment(sketch, "E132.MirrorCS", {"start": v(1221.74, 1908.81) * mm, "end": v(2.54, 1908.81) * mm});
            skLineSegment(sketch, "E133.MirrorCS", {"start": v(1221.74, 1482.1) * mm, "end": v(2.54, 1482.1) * mm});
            skLineSegment(sketch, "E134.MirrorCS", {"start": v(1221.74, 364.5) * mm, "end": v(2.54, 364.5) * mm});
            skLineSegment(sketch, "E135.MirrorCS", {"start": v(1221.74, 1322.07) * mm, "end": v(2.54, 1322.07) * mm});
            skLineSegment(sketch, "E136.MirrorCS", {"start": v(1221.74, 1055.37) * mm, "end": v(2.54, 1055.37) * mm});
            skLineSegment(sketch, "E137.MirrorCS", {"start": v(1221.74, 2498.09) * mm, "end": v(2.54, 2498.09) * mm});
            skLineSegment(sketch, "E138.MirrorCS", {"start": v(1221.74, 628.65) * mm, "end": v(2.54, 628.65) * mm});
            skLineSegment(sketch, "E139.MirrorCS", {"start": v(1221.74, 575.31) * mm, "end": v(2.54, 575.31) * mm});
            skLineSegment(sketch, "E140.MirrorCS", {"start": v(1221.74, 895.35) * mm, "end": v(2.54, 895.35) * mm});
            skLineSegment(sketch, "E141.MirrorCS", {"start": v(1221.74, 2284.73) * mm, "end": v(2.54, 2284.73) * mm});
            skLineSegment(sketch, "E142.MirrorCS", {"start": v(1221.74, 1591.31) * mm, "end": v(2.54, 1591.31) * mm});
            skLineSegment(sketch, "E143.MirrorCS", {"start": v(1221.74, -8.89) * mm, "end": v(2.54, -8.89) * mm});
            skLineSegment(sketch, "E144.MirrorCS", {"start": v(1221.74, 97.8) * mm, "end": v(2.54, 97.8) * mm});
            skLineSegment(sketch, "E145.MirrorCS", {"start": v(1221.74, 2231.39) * mm, "end": v(2.54, 2231.39) * mm});
            skLineSegment(sketch, "E146.MirrorCS", {"start": v(1221.74, 1855.47) * mm, "end": v(2.54, 1855.47) * mm});
            skLineSegment(sketch, "E147.MirrorCS", {"start": v(1221.74, 2338.07) * mm, "end": v(2.54, 2338.07) * mm});
            skLineSegment(sketch, "E148.MirrorCS", {"start": v(1221.74, 1057.91) * mm, "end": v(2.54, 1057.91) * mm});
            skLineSegment(sketch, "E149.MirrorCS", {"start": v(1221.74, 2122.17) * mm, "end": v(2.54, 2122.17) * mm});
            skLineSegment(sketch, "E150.MirrorCS", {"start": v(1221.74, 1537.97) * mm, "end": v(2.54, 1537.97) * mm});
            skLineSegment(sketch, "E151.MirrorCS", {"start": v(1221.74, 2391.4) * mm, "end": v(2.54, 2391.4) * mm});
            skLineSegment(sketch, "E152.MirrorCS", {"start": v(1221.74, 44.45) * mm, "end": v(2.54, 44.45) * mm});
            skLineSegment(sketch, "E153.MirrorCS", {"start": v(1221.74, 1164.6) * mm, "end": v(2.54, 1164.6) * mm});
            skLineSegment(sketch, "E154.MirrorCS", {"start": v(1221.74, 791.21) * mm, "end": v(2.54, 791.21) * mm});
            skLineSegment(sketch, "E155.MirrorCS", {"start": v(1221.74, 951.23) * mm, "end": v(2.54, 951.23) * mm});
            skLineSegment(sketch, "E156.MirrorCS", {"start": v(1221.74, 417.83) * mm, "end": v(2.54, 417.83) * mm});
            skLineSegment(sketch, "E157.MirrorCS", {"start": v(1221.74, 2018.03) * mm, "end": v(2.54, 2018.03) * mm});
            skLineSegment(sketch, "E158.MirrorCS", {"start": v(1221.74, 204.47) * mm, "end": v(2.54, 204.47) * mm});
            skLineSegment(sketch, "E159.MirrorCS", {"start": v(1221.74, 1111.25) * mm, "end": v(2.54, 1111.25) * mm});
            skLineSegment(sketch, "E160.MirrorCS", {"start": v(1221.74, 1324.61) * mm, "end": v(2.54, 1324.61) * mm});
            skLineSegment(sketch, "E161.MirrorCS", {"start": v(1221.74, 2071.37) * mm, "end": v(2.54, 2071.37) * mm});
            skLineSegment(sketch, "E162.MirrorCS", {"start": v(1221.74, 2388.87) * mm, "end": v(2.54, 2388.87) * mm});
            skLineSegment(sketch, "E163.MirrorCS", {"start": v(1221.74, 1484.63) * mm, "end": v(2.54, 1484.63) * mm});
            skLineSegment(sketch, "E164.MirrorCS", {"start": v(1221.74, 41.91) * mm, "end": v(2.54, 41.91) * mm});
            skLineSegment(sketch, "E165.MirrorCS", {"start": v(1221.74, 1644.65) * mm, "end": v(2.54, 1644.65) * mm});
            skLineSegment(sketch, "E166.MirrorCS", {"start": v(1221.74, 2442.2) * mm, "end": v(2.54, 2442.2) * mm});
            skLineSegment(sketch, "E167.MirrorCS", {"start": v(1221.74, 631.2) * mm, "end": v(2.54, 631.2) * mm});
            skLineSegment(sketch, "E168.MirrorCS", {"start": v(1221.74, 1217.93) * mm, "end": v(2.54, 1217.93) * mm});
            skLineSegment(sketch, "E169.MirrorCS", {"start": v(1221.74, 1271.27) * mm, "end": v(2.54, 1271.27) * mm});
            skLineSegment(sketch, "E170.MirrorCS", {"start": v(1221.74, 1698) * mm, "end": v(2.54, 1698) * mm});
            skLineSegment(sketch, "E171.MirrorCS", {"start": v(1221.74, 1751.33) * mm, "end": v(2.54, 1751.33) * mm});
            skLineSegment(sketch, "E172.MirrorCS", {"start": v(1221.74, 1911.35) * mm, "end": v(2.54, 1911.35) * mm});
            skLineSegment(sketch, "E173.MirrorCS", {"start": v(1221.74, 897.9) * mm, "end": v(2.54, 897.9) * mm});
            skLineSegment(sketch, "E174.MirrorCS", {"start": v(1221.74, 1377.95) * mm, "end": v(2.54, 1377.95) * mm});
            skLineSegment(sketch, "E175.MirrorCS", {"start": v(1221.74, 2124.7) * mm, "end": v(2.54, 2124.7) * mm});
            skLineSegment(sketch, "E176.MirrorCS", {"start": v(1221.74, 684.53) * mm, "end": v(2.54, 684.53) * mm});
            skLineSegment(sketch, "E177.MirrorCS", {"start": v(1221.74, 2498.09) * mm, "end": v(1221.74, 2498.09) * mm});
            skLineSegment(sketch, "E178.MirrorCS", {"start": v(1221.74, 2178.05) * mm, "end": v(2.54, 2178.05) * mm});
            skLineSegment(sketch, "E179.MirrorCS", {"start": v(1221.74, 524.51) * mm, "end": v(2.54, 524.51) * mm});
            skLineSegment(sketch, "E180.MirrorCS", {"start": v(1221.74, 257.81) * mm, "end": v(2.54, 257.81) * mm});
            skLineSegment(sketch, "E181.MirrorCS", {"start": v(1221.74, 2548.89) * mm, "end": v(2.54, 2548.89) * mm});
            skLineSegment(sketch, "E182.MirrorCS", {"start": v(1221.74, 2495.55) * mm, "end": v(2.54, 2495.55) * mm});
            skLineSegment(sketch, "E183.MirrorCS", {"start": v(1221.74, 1804.67) * mm, "end": v(2.54, 1804.67) * mm});
            skLineSegment(sketch, "E184.MirrorCS", {"start": v(1221.74, 844.55) * mm, "end": v(2.54, 844.55) * mm});
            skLineSegment(sketch, "E185.MirrorCS", {"start": v(1221.74, 1004.57) * mm, "end": v(2.54, 1004.57) * mm});
            skLineSegment(sketch, "E186.MirrorCS", {"start": v(1221.74, 1858) * mm, "end": v(2.54, 1858.01) * mm});
            skLineSegment(sketch, "E187.MirrorCS", {"start": v(1221.74, 311.15) * mm, "end": v(2.54, 311.15) * mm});
            skLineSegment(sketch, "E188.MirrorCS", {"start": v(1221.74, 1964.69) * mm, "end": v(2.54, 1964.7) * mm});
            skLineSegment(sketch, "E189.MirrorCS", {"start": v(1221.74, 737.87) * mm, "end": v(2.54, 737.87) * mm});
            skLineSegment(sketch, "E190.MirrorCS", {"start": v(1221.74, 361.95) * mm, "end": v(2.54, 361.95) * mm});
            skLineSegment(sketch, "E191.MirrorCS", {"start": v(1221.74, 1431.3) * mm, "end": v(2.54, 1431.3) * mm});
            skLineSegment(sketch, "E192.MirrorCS", {"start": v(1221.74, 948.7) * mm, "end": v(2.54, 948.7) * mm});
            skLineSegment(sketch, "E193.MirrorCS", {"start": v(1221.74, 148.6) * mm, "end": v(2.54, 148.6) * mm});
            skLineSegment(sketch, "E194.MirrorCS", {"start": v(1221.74, 577.85) * mm, "end": v(2.54, 577.85) * mm});
            skLineSegment(sketch, "E195.MirrorCS", {"start": v(1221.74, 471.17) * mm, "end": v(2.54, 471.17) * mm});
            skLineSegment(sketch, "E196.MirrorCS", {"start": v(1221.74, 1215.4) * mm, "end": v(2.54, 1215.4) * mm});
            skSolve(sketch);
        }
        {
            var Q0;
            Q0 = qSketchRegion(id + "F0", true);
            extrude(context, id + "F1", {"entities" : qUnion([Q0]), "depth" : 25.4 * mm, "offsetDistance" : 25.4 * mm});
        }
    });
